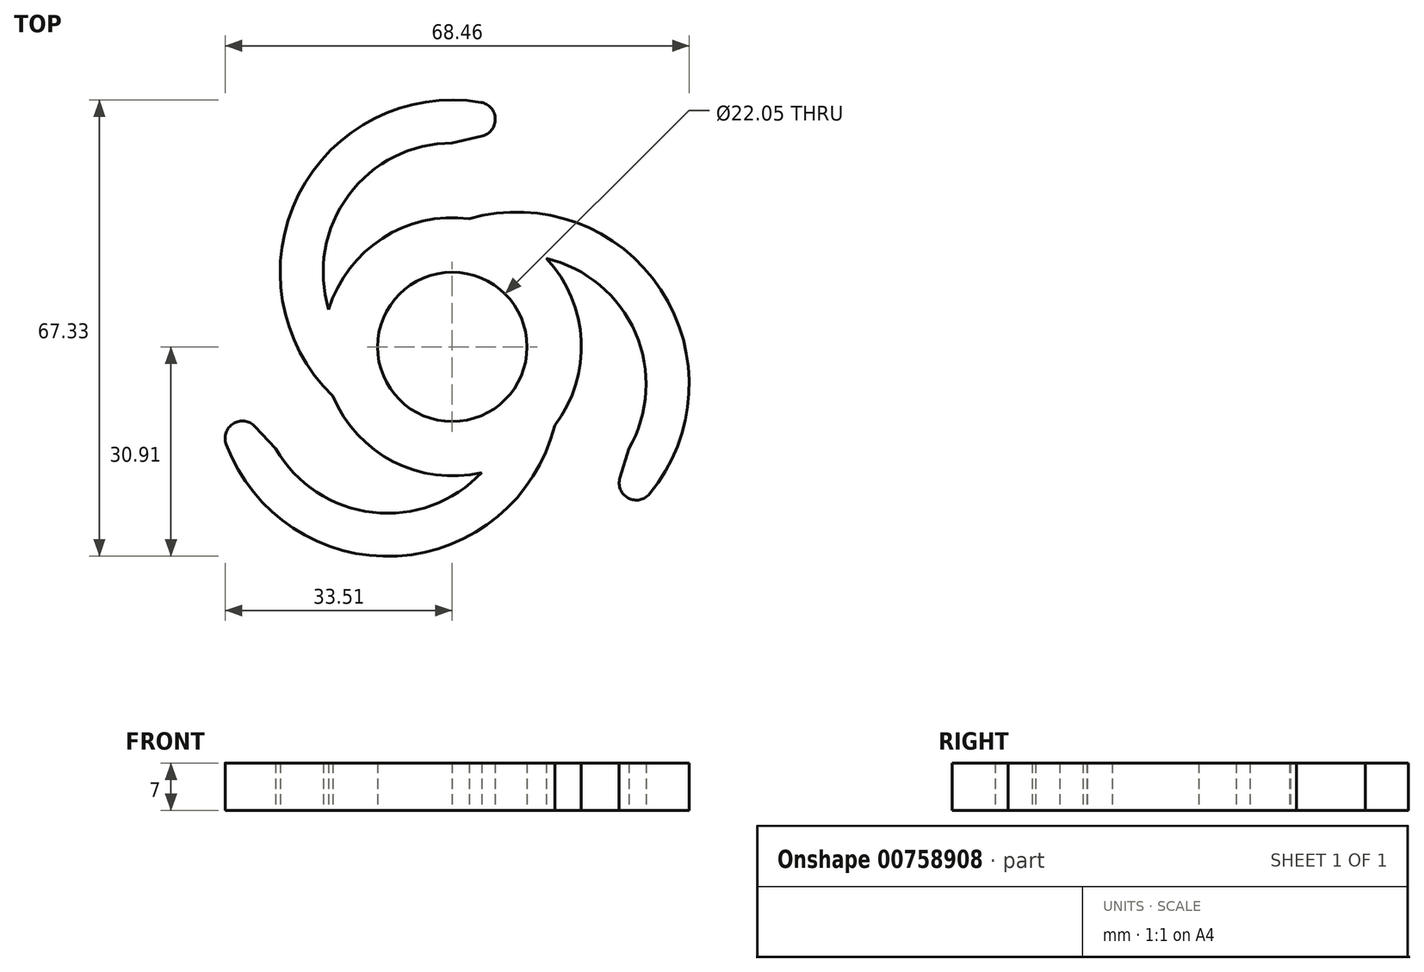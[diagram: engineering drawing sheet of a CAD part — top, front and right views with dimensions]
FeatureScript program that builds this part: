
annotation { "Feature Type Name" : "Feature", "Feature Type Description" : "" }
export const myFeature = defineFeature(function(context is Context, id is Id, definition is map)
    precondition{}
    {
        {
            var Q0;
            Q0=qCreatedBy(makeId("Top.planeOp"),FACE);
            var sketch = newSketch(context, id + "F0", { "sketchPlane" : qUnion([Q0])});
            skCircle(sketch, "E0", {"center": v(0, 0) * mm, "radius": 11.03 * mm});
            skLineSegment(sketch, "E1", {"start": v(-33.02, 0) * mm, "end": v(-11.03, 0) * mm, "construction": true});
            skLineSegment(sketch, "E2", {"start": v(0, 19.05) * mm, "end": v(0, 11.03) * mm, "construction": true});
            skArc(sketch, "E3", {"start": v(-17.6, -7.29) * mm, "mid": v(-8.7, -16.95) * mm, "end": v(4.34, -18.55) * mm});
            skArc(sketch, "E4", {"start": v(0, 30.07) * mm, "mid": v(-15.3, 22.38) * mm, "end": v(-18.23, 5.51) * mm});
            skLineSegment(sketch, "E5.trimOffspring", {"start": v(0, 0) * mm, "end": v(0, -11.03) * mm, "construction": true});
            skLineSegment(sketch, "E6.trimOffspring", {"start": v(11.03, 0) * mm, "end": v(33.02, 0) * mm, "construction": true});
            skPoint(sketch, "E7", {"position": v(0, 30.07) * mm});
            skArc(sketch, "E8.1.0", {"start": v(-26.05, -15.04) * mm, "mid": v(-11.73, -24.44) * mm, "end": v(4.34, -18.55) * mm});
            skArc(sketch, "E8.2.0", {"start": v(26.05, -15.04) * mm, "mid": v(27.03, 2.06) * mm, "end": v(13.9, 13.04) * mm});
            skArc(sketch, "E9.trimOffspring", {"start": v(-9.6, -5.43) * mm, "mid": v(-9.55, -5.46) * mm, "end": v(-9.5, -5.49) * mm});
            skArc(sketch, "E10.trimOffspring", {"start": v(-9.5, -5.49) * mm, "mid": v(-9.5, -5.54) * mm, "end": v(-9.5, -5.6) * mm});
            skPoint(sketch, "E11.orphan", {"position": v(-4.34, -18.55) * mm});
            skArc(sketch, "E12.trimOffspring", {"start": v(0, 10.97) * mm, "mid": v(-0.05, 11) * mm, "end": v(-0.1, 11.02) * mm});
            skPoint(sketch, "E13.orphan", {"position": v(-13.9, 13.04) * mm});
            skArc(sketch, "E14.trimOffspring", {"start": v(9.5, -5.49) * mm, "mid": v(9.55, -5.46) * mm, "end": v(9.6, -5.43) * mm});
            skPoint(sketch, "E15.orphan", {"position": v(18.23, 5.51) * mm});
            skArc(sketch, "E16", {"start": v(12.7, 33.02) * mm, "mid": v(-20.3, 26.29) * mm, "end": v(-17.6, -7.29) * mm});
            skLineSegment(sketch, "E17", {"start": v(0, 11.02) * mm, "end": v(12.7, 33.02) * mm, "construction": true});
            skLineSegment(sketch, "E18", {"start": v(0, 30.08) * mm, "end": v(12.7, 33.02) * mm});
            skArc(sketch, "E19.1.0", {"start": v(-34.95, -5.51) * mm, "mid": v(-12.61, -30.73) * mm, "end": v(15.11, -11.6) * mm});
            skLineSegment(sketch, "E19.1.1", {"start": v(-26.05, -15.04) * mm, "end": v(-34.95, -5.51) * mm});
            skArc(sketch, "E19.2.0", {"start": v(22.25, -27.5) * mm, "mid": v(32.92, 4.44) * mm, "end": v(2.49, 18.89) * mm});
            skLineSegment(sketch, "E19.2.1", {"start": v(26.05, -15.04) * mm, "end": v(22.25, -27.5) * mm});
            skArc(sketch, "E20.trimOffspring", {"start": v(9.5, -5.6) * mm, "mid": v(9.5, -5.54) * mm, "end": v(9.5, -5.49) * mm});
            skArc(sketch, "E21.trimOffspring", {"start": v(0.1, 11.02) * mm, "mid": v(0.05, 11) * mm, "end": v(0, 10.97) * mm});
            skArc(sketch, "E22.trimOffspring", {"start": v(4.34, 18.55) * mm, "mid": v(-9.52, 16.5) * mm, "end": v(-18.23, 5.51) * mm});
            skArc(sketch, "E23.trimOffspring", {"start": v(15.11, -11.6) * mm, "mid": v(19.03, 0.94) * mm, "end": v(13.9, 13.04) * mm});
            skSolve(sketch);
        }
        {
            var Q0;
            Q0=makeQuery(id+"F0.imprint","IMPRINT",FACE,{"disambiguationData":[TD([[makeQuery(id+"F0.imprint","IMPRINT",EDGE,{"derivedFrom":sQuery(id+"F0.wireOp",EDGE,"E0")}),-1.0]])]});
            var Q1;
            {var subQ0=sQuery(id+"F0.wireOp",EDGE,"KKeOOKYj-ovYi-SoW4-MspW-oF9TwUzpAegU");Q1=makeQuery(id+"F0.imprint","IMPRINT",FACE,{"disambiguationData":[TD([[makeQuery(id+"F0.imprint","IMPRINT",EDGE,{"derivedFrom":subQ0}),-1.0]])]});}
            var Q2;
            {var subQ0=sQuery(id+"F0.wireOp",EDGE,"25e1cfba-f07b-4f7d-a427-730f02031464.1.1");Q2=makeQuery(id+"F0.imprint","IMPRINT",FACE,{"disambiguationData":[TD([[makeQuery(id+"F0.imprint","IMPRINT",EDGE,{"derivedFrom":subQ0}),-1.0]])]});}
            var Q3;
            {var subQ0=sQuery(id+"F0.wireOp",EDGE,"zxYjU2Gi-UagP-9GxD-yehC-1jQG6XL1JYtI");var subQ1=sQuery(id+"F0.wireOp",EDGE,"E3");var subQ2=makeQuery(id+"F0.imprint","INTERSECT",VERTEX,{"disambiguationData":[OD(0.0)],"derivedFrom":[subQ1,subQ0]});Q3=makeQuery(id+"F0.imprint","IMPRINT",FACE,{"disambiguationData":[TD([[makeQuery(id+"F0.imprint","IMPRINT",EDGE,{"disambiguationData":[TD([[subQ2,1.0]])],"derivedFrom":subQ1}),1.0]])]});}
            var Q4;
            {var subQ0=sQuery(id+"F0.wireOp",EDGE,"25e1cfba-f07b-4f7d-a427-730f02031464.1.0");var subQ1=sQuery(id+"F0.wireOp",EDGE,"E3");var subQ2=makeQuery(id+"F0.imprint","INTERSECT",VERTEX,{"disambiguationData":[OD(0.0)],"derivedFrom":[subQ1,subQ0]});Q4=makeQuery(id+"F0.imprint","IMPRINT",FACE,{"disambiguationData":[TD([[makeQuery(id+"F0.imprint","IMPRINT",EDGE,{"disambiguationData":[TD([[subQ2,1.0]])],"derivedFrom":subQ1}),1.0]])]});}
            extrude(context, id + "F1", {"entities" : qUnion([Q0, Q1, Q2, Q3, Q4]), "depth" : 7 * mm, "offsetDistance" : 25.4 * mm});
        }
        {
            var Q0;
            Q0=makeQuery(id+"F1.opExtrude","SWEPT_EDGE",EDGE,{"disambiguationData":[OSD([sQuery(id+"F0.wireOp",EDGE,"E16"),sQuery(id+"F0.wireOp",EDGE,"E18")])]});
            var Q1;
            Q1=makeQuery(id+"F1.opExtrude","SWEPT_EDGE",EDGE,{"disambiguationData":[OSD([sQuery(id+"F0.wireOp",EDGE,"E19.2.0"),sQuery(id+"F0.wireOp",EDGE,"E19.2.1")])]});
            var Q2;
            Q2=makeQuery(id+"F1.opExtrude","SWEPT_EDGE",EDGE,{"disambiguationData":[OSD([sQuery(id+"F0.wireOp",EDGE,"E19.1.0"),sQuery(id+"F0.wireOp",EDGE,"E19.1.1")])]});
            fillet(context, id + "F2", {"entities" : qUnion([Q0, Q1, Q2]), "radius" : 2.54 * mm, "tangentPropagation" : true, "allowEdgeOverflow" : false});
        }
    });
